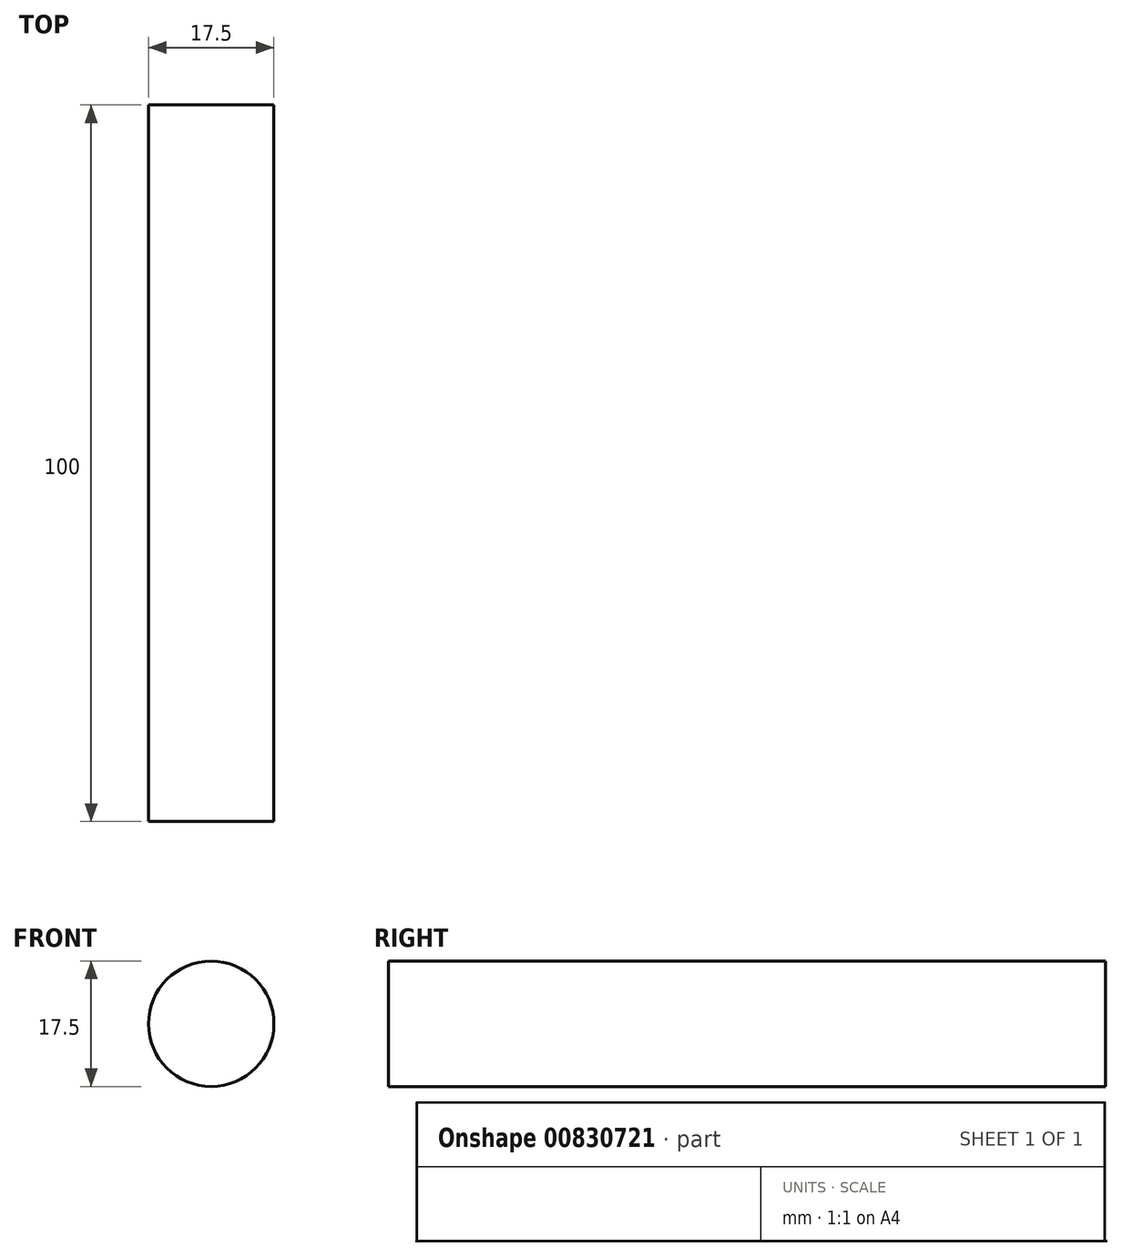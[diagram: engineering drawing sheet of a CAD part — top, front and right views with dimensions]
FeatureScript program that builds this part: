
annotation { "Feature Type Name" : "Feature", "Feature Type Description" : "" }
export const myFeature = defineFeature(function(context is Context, id is Id, definition is map)
    precondition{}
    {
        {
            assignVariable(context, id + "F0", {"name" : "RodLength", "anyValue" : 100});
        }
        {
            var Q0;
            Q0=qCreatedBy(makeId("Front.planeOp"),FACE);
            var sketch = newSketch(context, id + "F1", { "sketchPlane" : qUnion([Q0])});
            skCircle(sketch, "E0", {"center": v(0, 0) * mm, "radius": 8.75 * mm});
            skSolve(sketch);
        }
        {
            var Q0;
            Q0=makeQuery(id+"F1.imprint","IMPRINT",FACE,{"disambiguationData":[TD([[makeQuery(id+"F1.imprint","IMPRINT",EDGE,{"derivedFrom":sQuery(id+"F1.wireOp",EDGE,"E0")}),1.0]])]});
            extrude(context, id + "F2", {"entities" : qUnion([Q0]), "endBound" : BoundingType.SYMMETRIC, "depth" : (getVariable(context, 'RodLength')) * mm, "offsetDistance" : 25 * mm});
        }
        {
            var Q0;
            Q0=makeQuery(id+"F2.opExtrude","SWEPT_BODY",BODY,{"disambiguationData":[OSD([sQuery(id+"F1.wireOp",EDGE,"E0")])]});
            transform(context, id + "F3", {"entities" : qUnion([Q0]), "transformType" : TransformType.TRANSLATION_3D, "dx" : 0 * mm, "dy" : 0 * mm, "dz" : 0 * mm, "makeCopy" : true});
        }
    });
